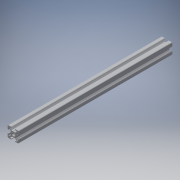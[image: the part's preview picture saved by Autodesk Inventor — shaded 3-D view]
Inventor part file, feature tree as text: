
AUTODESK INVENTOR PART (.ipt)
format: ipt  version: 2019 (Build 230136000, 136)  size: 309,248 bytes
history: native  units: in
note: dims shown in document units (in); Inventor stores cm internally (conversion verified against a paired STEP export)
features: other x3, extrude x1, sketch x1
ambient origin geometry x8: Origin, YZ Plane, XZ Plane, XY Plane, X Axis, Y Axis, Z Axis, Center Point
bodies: Solid1 (feature_tree)
feature tree (5):
  other  "Blocks"
  extrude  "Extrusion1"  Depth=1.0in
  sketch  "Sketch1"  dims[d1=0.0in d13=1.0in d14=1.0in]
  other  "20x20"
  other  "20x20:1"
